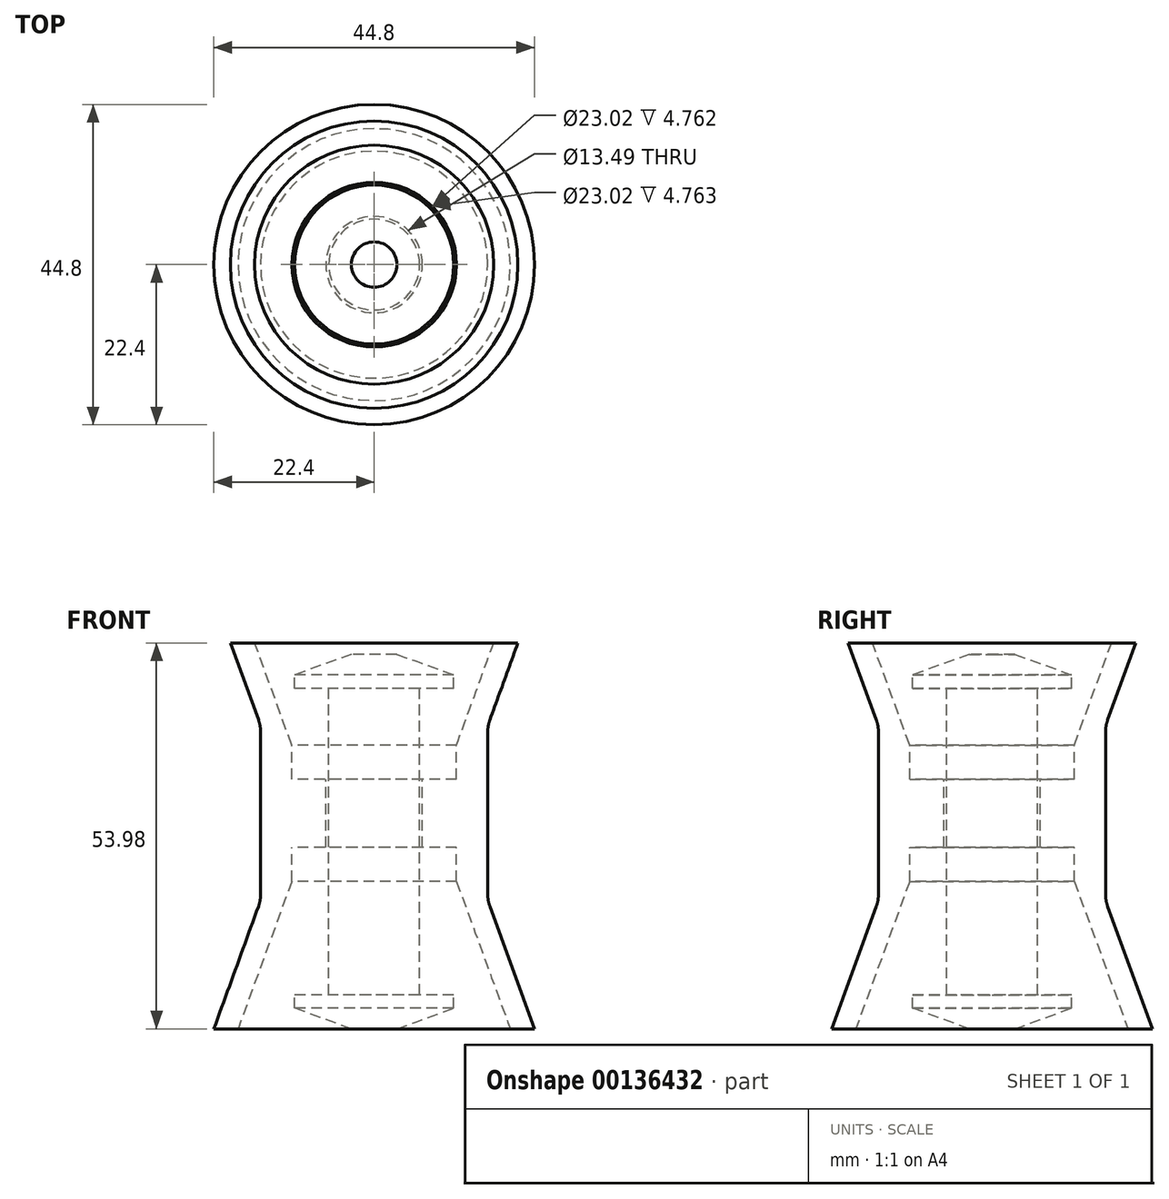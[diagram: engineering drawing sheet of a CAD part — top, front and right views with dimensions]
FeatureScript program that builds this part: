
annotation { "Feature Type Name" : "Feature", "Feature Type Description" : "" }
export const myFeature = defineFeature(function(context is Context, id is Id, definition is map)
    precondition{}
    {
        {
            var Q0;
            Q0=qCreatedBy(makeId("Front.planeOp"),FACE);
            var sketch = newSketch(context, id + "F0", { "sketchPlane" : qUnion([Q0])});
            skLineSegment(sketch, "E0", {"start": v(0, 0) * mm, "end": v(3.17, 0) * mm});
            skLineSegment(sketch, "E1", {"start": v(3.17, 0) * mm, "end": v(11.11, 2.89) * mm});
            skLineSegment(sketch, "E2", {"start": v(11.11, 2.89) * mm, "end": v(11.11, 4.76) * mm});
            skCircle(sketch, "E3", {"center": v(0, 21.28) * mm, "radius": 21.08 * mm, "construction": true});
            skLineSegment(sketch, "E4", {"start": v(0, 0) * mm, "end": v(0, 52.39) * mm});
            skLineSegment(sketch, "E5", {"start": v(0, 0) * mm, "end": v(0, -15.55) * mm, "construction": true});
            skLineSegment(sketch, "E6", {"start": v(0, 52.39) * mm, "end": v(3.17, 52.39) * mm});
            skLineSegment(sketch, "E7", {"start": v(3.17, 52.39) * mm, "end": v(11.11, 49.5) * mm});
            skLineSegment(sketch, "E8", {"start": v(11.11, 49.5) * mm, "end": v(11.11, 47.62) * mm});
            skLineSegment(sketch, "E9", {"start": v(11.11, 47.62) * mm, "end": v(6.35, 47.62) * mm});
            skLineSegment(sketch, "E10", {"start": v(6.35, 47.62) * mm, "end": v(6.35, 4.76) * mm});
            skLineSegment(sketch, "E11", {"start": v(6.35, 4.76) * mm, "end": v(11.11, 4.76) * mm});
            skLineSegment(sketch, "E12", {"start": v(-22.4, 0) * mm, "end": v(-19.02, 0) * mm});
            skLineSegment(sketch, "E13", {"start": v(-19.02, 0) * mm, "end": v(-11.5, 20.64) * mm});
            skLineSegment(sketch, "E14", {"start": v(-11.5, 20.64) * mm, "end": v(-11.5, 25.4) * mm});
            skLineSegment(sketch, "E15", {"start": v(-11.5, 25.4) * mm, "end": v(-6.75, 25.4) * mm});
            skLineSegment(sketch, "E16", {"start": v(-6.75, 25.4) * mm, "end": v(-6.75, 34.92) * mm});
            skLineSegment(sketch, "E17", {"start": v(-6.75, 34.92) * mm, "end": v(-11.5, 34.92) * mm});
            skLineSegment(sketch, "E18", {"start": v(-11.5, 34.92) * mm, "end": v(-11.5, 39.69) * mm});
            skLineSegment(sketch, "E19", {"start": v(-11.5, 39.69) * mm, "end": v(-16.7, 53.97) * mm});
            skLineSegment(sketch, "E20", {"start": v(-16.7, 53.97) * mm, "end": v(-20.09, 53.97) * mm});
            skLineSegment(sketch, "E21", {"start": v(-20.09, 53.97) * mm, "end": v(-15.88, 42.4) * mm});
            skLineSegment(sketch, "E22", {"start": v(-15.88, 42.4) * mm, "end": v(-15.88, 17.93) * mm});
            skLineSegment(sketch, "E23", {"start": v(-15.88, 17.93) * mm, "end": v(-22.4, 0) * mm});
            skSolve(sketch);
        }
        {
            var Q0;
            Q0 = qSketchRegion(id + "F0", true);
            var Q1;
            Q1=sQuery(id+"F0.wireOp",EDGE,"E5");
            revolve(context, id + "F1", {"entities" : qUnion([Q0]), "axis" : qUnion([Q1]), "revolveType" : RevolveType.FULL});
        }
        {
            var Q0;
            Q0=makeQuery(id+"F1.opRevolve","SWEPT_EDGE",EDGE,{"disambiguationData":[OSD([sQuery(id+"F0.wireOp",EDGE,"E21"),sQuery(id+"F0.wireOp",EDGE,"E22")])]});
            var Q1;
            Q1=makeQuery(id+"F1.opRevolve","SWEPT_EDGE",EDGE,{"disambiguationData":[OSD([sQuery(id+"F0.wireOp",EDGE,"E22"),sQuery(id+"F0.wireOp",EDGE,"E23")])]});
            fillet(context, id + "F2", {"entities" : qUnion([Q0, Q1]), "radius" : 4.76 * mm, "tangentPropagation" : true, "allowEdgeOverflow" : false});
        }
    });
